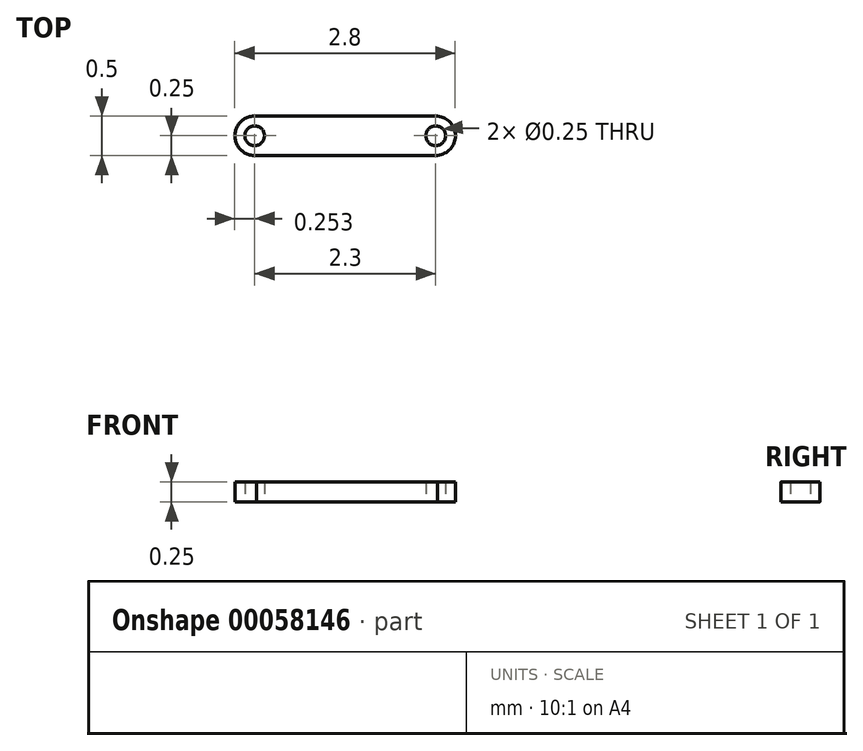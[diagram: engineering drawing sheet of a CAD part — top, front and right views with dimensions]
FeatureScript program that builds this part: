
annotation { "Feature Type Name" : "Feature", "Feature Type Description" : "" }
export const myFeature = defineFeature(function(context is Context, id is Id, definition is map)
    precondition{}
    {
        {
            var Q0;
            Q0=qCreatedBy(makeId("Top.planeOp"),FACE);
            var sketch = newSketch(context, id + "F0", { "sketchPlane" : qUnion([Q0])});
            skArc(sketch, "E0", {"start": v(-35.64, 0.25) * mm, "mid": v(-35.92, 0) * mm, "end": v(-35.64, -0.25) * mm});
            skArc(sketch, "E1", {"start": v(-33.4, -0.25) * mm, "mid": v(-33.12, 0) * mm, "end": v(-33.4, 0.25) * mm});
            skCircle(sketch, "E2", {"center": v(-35.67, 0) * mm, "radius": 0.13 * mm});
            skCircle(sketch, "E3", {"center": v(-33.37, 0) * mm, "radius": 0.13 * mm});
            skLineSegment(sketch, "E4", {"start": v(-35.7, 0.25) * mm, "end": v(-33.34, 0.25) * mm});
            skLineSegment(sketch, "E5", {"start": v(-35.7, -0.25) * mm, "end": v(-33.34, -0.25) * mm});
            skSolve(sketch);
        }
        {
            var Q0;
            {var subQ0=sQuery(id+"F0.wireOp",EDGE,"E4");var subQ1=sQuery(id+"F0.wireOp",EDGE,"E0");var subQ2=makeQuery(id+"F0.imprint","INTERSECT",VERTEX,{"disambiguationData":[OD(0.0)],"derivedFrom":[subQ1,subQ0]});Q0=makeQuery(id+"F0.imprint","IMPRINT",FACE,{"disambiguationData":[TD([[makeQuery(id+"F0.imprint","IMPRINT",EDGE,{"disambiguationData":[TD([[subQ2,-1.0]])],"derivedFrom":subQ1}),1.0]])]});}
            var Q1;
            {var subQ0=sQuery(id+"F0.wireOp",EDGE,"E5");var subQ1=sQuery(id+"F0.wireOp",EDGE,"E0");var subQ2=makeQuery(id+"F0.imprint","INTERSECT",VERTEX,{"disambiguationData":[OD(0.0)],"derivedFrom":[subQ1,subQ0]});Q1=makeQuery(id+"F0.imprint","IMPRINT",FACE,{"disambiguationData":[TD([[makeQuery(id+"F0.imprint","IMPRINT",EDGE,{"disambiguationData":[TD([[subQ2,1.0]])],"derivedFrom":subQ1}),1.0]])]});}
            var Q2;
            {var subQ0=sQuery(id+"F0.wireOp",EDGE,"E5");var subQ1=sQuery(id+"F0.wireOp",EDGE,"E1");var subQ2=makeQuery(id+"F0.imprint","INTERSECT",VERTEX,{"disambiguationData":[OD(0.0)],"derivedFrom":[subQ1,subQ0]});Q2=makeQuery(id+"F0.imprint","IMPRINT",FACE,{"disambiguationData":[TD([[makeQuery(id+"F0.imprint","IMPRINT",EDGE,{"disambiguationData":[TD([[subQ2,-1.0]])],"derivedFrom":subQ1}),1.0]])]});}
            var Q3;
            {var subQ0=sQuery(id+"F0.wireOp",EDGE,"E4");var subQ1=sQuery(id+"F0.wireOp",EDGE,"E1");var subQ2=makeQuery(id+"F0.imprint","INTERSECT",VERTEX,{"disambiguationData":[OD(0.0)],"derivedFrom":[subQ1,subQ0]});Q3=makeQuery(id+"F0.imprint","IMPRINT",FACE,{"disambiguationData":[TD([[makeQuery(id+"F0.imprint","IMPRINT",EDGE,{"disambiguationData":[TD([[subQ2,1.0]])],"derivedFrom":subQ1}),1.0]])]});}
            var Q4;
            Q4=makeQuery(id+"F0.imprint","IMPRINT",FACE,{"disambiguationData":[TD([[makeQuery(id+"F0.imprint","IMPRINT",EDGE,{"derivedFrom":sQuery(id+"F0.wireOp",EDGE,"E2")}),-1.0]])]});
            extrude(context, id + "F1", {"entities" : qUnion([Q0, Q1, Q2, Q3, Q4]), "depth" : 0.25 * mm});
        }
    });
